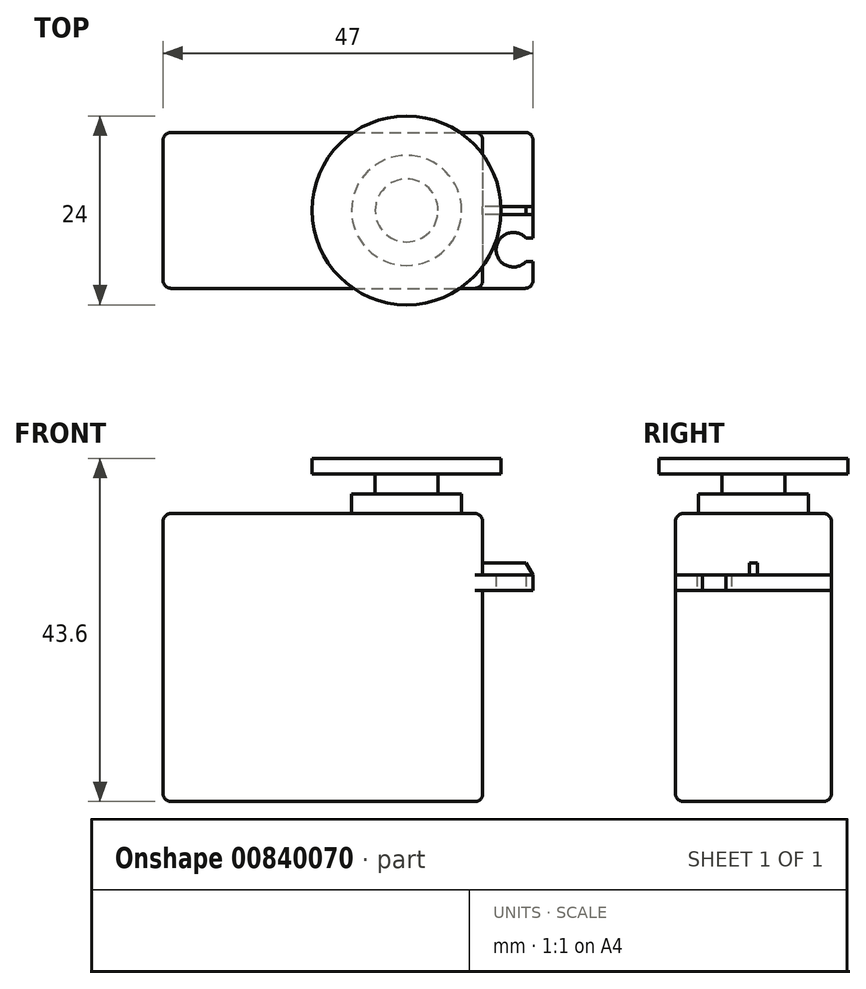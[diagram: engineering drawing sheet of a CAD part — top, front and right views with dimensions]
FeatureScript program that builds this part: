
annotation { "Feature Type Name" : "Feature", "Feature Type Description" : "" }
export const myFeature = defineFeature(function(context is Context, id is Id, definition is map)
    precondition{}
    {
        {
            var Q0;
            Q0=qCreatedBy(makeId("Top.planeOp"),FACE);
            cPlane(context, id + "F0", {"entities" : qUnion([Q0]), "cplaneType" : CPlaneType.OFFSET, "offset" : 26.8 * mm, "width" : 150 * mm, "height" : 150 * mm});
        }
        {
            var Q0;
            Q0=qCreatedBy(makeId("Top.planeOp"),FACE);
            var sketch = newSketch(context, id + "F1", { "sketchPlane" : qUnion([Q0])});
            skLineSegment(sketch, "E0.bottom", {"start": v(-20.3, 9.9) * mm, "end": v(20.3, 9.9) * mm});
            skLineSegment(sketch, "E0.top", {"start": v(-20.3, -9.9) * mm, "end": v(20.3, -9.9) * mm});
            skLineSegment(sketch, "E0.left", {"start": v(-20.3, 9.9) * mm, "end": v(-20.3, -9.9) * mm});
            skLineSegment(sketch, "E0.right", {"start": v(20.3, 9.9) * mm, "end": v(20.3, -9.9) * mm});
            skSolve(sketch);
        }
        {
            var Q0;
            Q0=makeQuery(id+"F1.imprint","IMPRINT",FACE,{"disambiguationData":[TD([[makeQuery(id+"F1.imprint","IMPRINT",EDGE,{"derivedFrom":sQuery(id+"F1.wireOp",EDGE,"E0.bottom")}),-1.0]])]});
            extrude(context, id + "F2", {"entities" : qUnion([Q0]), "depth" : 36.6 * mm, "offsetDistance" : 25 * mm});
        }
        {
            var Q0;
            Q0=makeQuery(id+"F2.opExtrude","CAP_FACE",FACE,{"disambiguationData":[OSD([sQuery(id+"F1.wireOp",EDGE,"E0.bottom"),sQuery(id+"F1.wireOp",EDGE,"E0.top"),sQuery(id+"F1.wireOp",EDGE,"E0.left"),sQuery(id+"F1.wireOp",EDGE,"E0.right")])],"isStart":false});
            var sketch = newSketch(context, id + "F3", { "sketchPlane" : qUnion([Q0])});
            skCircle(sketch, "E1", {"center": v(10.64, 0) * mm, "radius": 7 * mm});
            skSolve(sketch);
        }
        {
            var Q0;
            Q0 = qSketchRegion(id + "F3", true);
            extrude(context, id + "F4", {"entities" : qUnion([Q0]), "operationType" : NewBodyOperationType.ADD, "depth" : 2.5 * mm, "offsetDistance" : 25 * mm});
        }
        {
            var Q0;
            Q0=makeQuery(id+"F4.opExtrude","CAP_FACE",FACE,{"disambiguationData":[OSD([sQuery(id+"F3.wireOp",EDGE,"E1")])],"isStart":false});
            var sketch = newSketch(context, id + "F5", { "sketchPlane" : qUnion([Q0])});
            skCircle(sketch, "E2", {"center": v(10.64, 0) * mm, "radius": 4 * mm});
            skSolve(sketch);
        }
        {
            var Q0;
            Q0 = qSketchRegion(id + "F5", true);
            extrude(context, id + "F6", {"entities" : qUnion([Q0]), "operationType" : NewBodyOperationType.ADD, "depth" : 2.5 * mm, "offsetDistance" : 25 * mm});
        }
        {
            var Q0;
            Q0=makeQuery(id+"F6.opExtrude","CAP_FACE",FACE,{"disambiguationData":[OSD([sQuery(id+"F5.wireOp",EDGE,"E2")])],"isStart":false});
            var sketch = newSketch(context, id + "F7", { "sketchPlane" : qUnion([Q0])});
            skCircle(sketch, "E3", {"center": v(10.64, 0) * mm, "radius": 12 * mm});
            skSolve(sketch);
        }
        {
            var Q0;
            Q0 = qSketchRegion(id + "F7", true);
            extrude(context, id + "F8", {"entities" : qUnion([Q0]), "operationType" : NewBodyOperationType.ADD, "depth" : 2 * mm, "offsetDistance" : 25 * mm});
        }
        {
            var Q0;
            {var subQ0=sQuery(id+"F1.wireOp",EDGE,"E0.bottom");var subQ1=sQuery(id+"F1.wireOp",EDGE,"E0.right");var subQ2=sQuery(id+"F1.wireOp",EDGE,"E0.top");Q0=makeQuery(id+"F11.boolean.opBoolean","SPLIT",FACE,{"disambiguationData":[TD([makeQuery(id+"F2.opExtrude","CAP_FACE",FACE,{"disambiguationData":[OSD([subQ0,subQ2,sQuery(id+"F1.wireOp",EDGE,"E0.left"),subQ1])],"isStart":true})])],"derivedFrom":makeQuery(id+"F2.opExtrude","SWEPT_FACE",FACE,{"disambiguationData":[OSD([subQ1])]})});}
            cPlane(context, id + "F9", {"entities" : qUnion([Q0]), "cplaneType" : CPlaneType.OFFSET, "offset" : 0 * mm, "width" : 150 * mm, "height" : 150 * mm});
        }
        {
            var Q0;
            Q0=qCreatedBy(id+"F0.planeOp",FACE);
            var sketch = newSketch(context, id + "F10", { "sketchPlane" : qUnion([Q0])});
            skLineSegment(sketch, "E4.bottom", {"start": v(20.3, 9.9) * mm, "end": v(26.7, 9.9) * mm});
            skLineSegment(sketch, "E4.top", {"start": v(20.3, -9.9) * mm, "end": v(26.7, -9.9) * mm});
            skLineSegment(sketch, "E4.left", {"start": v(20.3, 9.9) * mm, "end": v(20.3, -9.9) * mm});
            skLineSegment(sketch, "E4.right", {"start": v(26.7, 9.9) * mm, "end": v(26.7, -9.9) * mm});
            skSolve(sketch);
        }
        {
            var Q0;
            Q0 = qSketchRegion(id + "F10", true);
            extrude(context, id + "F11", {"entities" : qUnion([Q0]), "operationType" : NewBodyOperationType.ADD, "depth" : 2 * mm, "offsetDistance" : 25 * mm});
        }
        {
            var Q0;
            Q0=qCreatedBy(id+"F0.planeOp",FACE);
            var sketch = newSketch(context, id + "F12", { "sketchPlane" : qUnion([Q0])});
            skPoint(sketch, "E5", {"position": v(24.2, -5) * mm});
            skArc(sketch, "E6", {"start": v(25.8, -3.5) * mm, "mid": v(22, -5) * mm, "end": v(25.8, -6.5) * mm});
            skLineSegment(sketch, "E7", {"start": v(25.8, -3.5) * mm, "end": v(26.7, -3.5) * mm});
            skLineSegment(sketch, "E8", {"start": v(26.7, -3.5) * mm, "end": v(26.7, -6.5) * mm});
            skLineSegment(sketch, "E9", {"start": v(26.7, -6.5) * mm, "end": v(25.8, -6.5) * mm});
            skLineSegment(sketch, "E10", {"start": v(24.2, -5) * mm, "end": v(29.03, -5) * mm, "construction": true});
            skSolve(sketch);
        }
        {
            var Q0;
            Q0 = qSketchRegion(id + "F12", true);
            extrude(context, id + "F13", {"entities" : qUnion([Q0]), "operationType" : NewBodyOperationType.REMOVE, "depth" : 4 * mm, "offsetDistance" : 25 * mm});
        }
        {
            var Q0;
            {var subQ1=sQuery(id+"F1.wireOp",EDGE,"E0.left");var subQ2=sQuery(id+"F1.wireOp",EDGE,"E0.top");Q0=makeQuery(id+"FE7LxPU3QRs9F0V_1.1.F11.boolean.opBoolean","SPLIT",EDGE,{"disambiguationData":[TD([makeQuery(id+"F2.opExtrude","CAP_FACE",FACE,{"disambiguationData":[OSD([sQuery(id+"F1.wireOp",EDGE,"E0.bottom"),subQ2,subQ1,sQuery(id+"F1.wireOp",EDGE,"E0.right")])],"isStart":true})])],"derivedFrom":makeQuery(id+"F2.opExtrude","SWEPT_EDGE",EDGE,{"disambiguationData":[OSD([subQ2,subQ1])]})});}
            var Q1;
            Q1=makeQuery(id+"F2.opExtrude","CAP_EDGE",EDGE,{"disambiguationData":[OSD([sQuery(id+"F1.wireOp",EDGE,"E0.top")])],"isStart":true});
            var Q2;
            Q2=makeQuery(id+"F2.opExtrude","CAP_EDGE",EDGE,{"disambiguationData":[OSD([sQuery(id+"F1.wireOp",EDGE,"E0.left")])],"isStart":true});
            var Q3;
            {var subQ0=sQuery(id+"F1.wireOp",EDGE,"E0.left");var subQ2=sQuery(id+"F1.wireOp",EDGE,"E0.bottom");Q3=makeQuery(id+"FE7LxPU3QRs9F0V_1.1.F11.boolean.opBoolean","SPLIT",EDGE,{"disambiguationData":[TD([makeQuery(id+"F2.opExtrude","CAP_FACE",FACE,{"disambiguationData":[OSD([subQ2,sQuery(id+"F1.wireOp",EDGE,"E0.top"),subQ0,sQuery(id+"F1.wireOp",EDGE,"E0.right")])],"isStart":true})])],"derivedFrom":makeQuery(id+"F2.opExtrude","SWEPT_EDGE",EDGE,{"disambiguationData":[OSD([subQ2,subQ0])]})});}
            var Q4;
            Q4=makeQuery(id+"F2.opExtrude","CAP_EDGE",EDGE,{"disambiguationData":[OSD([sQuery(id+"F1.wireOp",EDGE,"E0.bottom")])],"isStart":true});
            var Q5;
            Q5=makeQuery(id+"F2.opExtrude","CAP_EDGE",EDGE,{"disambiguationData":[OSD([sQuery(id+"F1.wireOp",EDGE,"E0.right")])],"isStart":true});
            var Q6;
            {var subQ1=sQuery(id+"F1.wireOp",EDGE,"E0.right");var subQ2=sQuery(id+"F1.wireOp",EDGE,"E0.bottom");Q6=makeQuery(id+"F11.boolean.opBoolean","SPLIT",EDGE,{"disambiguationData":[TD([makeQuery(id+"F2.opExtrude","CAP_FACE",FACE,{"disambiguationData":[OSD([subQ2,sQuery(id+"F1.wireOp",EDGE,"E0.top"),sQuery(id+"F1.wireOp",EDGE,"E0.left"),subQ1])],"isStart":true})])],"derivedFrom":makeQuery(id+"F2.opExtrude","SWEPT_EDGE",EDGE,{"disambiguationData":[OSD([subQ2,subQ1])]})});}
            var Q7;
            {var subQ1=sQuery(id+"F1.wireOp",EDGE,"E0.right");var subQ2=sQuery(id+"F1.wireOp",EDGE,"E0.top");Q7=makeQuery(id+"F11.boolean.opBoolean","SPLIT",EDGE,{"disambiguationData":[TD([makeQuery(id+"F2.opExtrude","CAP_FACE",FACE,{"disambiguationData":[OSD([sQuery(id+"F1.wireOp",EDGE,"E0.bottom"),subQ2,sQuery(id+"F1.wireOp",EDGE,"E0.left"),subQ1])],"isStart":true})])],"derivedFrom":makeQuery(id+"F2.opExtrude","SWEPT_EDGE",EDGE,{"disambiguationData":[OSD([subQ2,subQ1])]})});}
            var Q8;
            {var subQ1=sQuery(id+"F1.wireOp",EDGE,"E0.left");var subQ2=sQuery(id+"F1.wireOp",EDGE,"E0.bottom");Q8=makeQuery(id+"FE7LxPU3QRs9F0V_1.1.F11.boolean.opBoolean","SPLIT",EDGE,{"disambiguationData":[TD([makeQuery(id+"F2.opExtrude","CAP_FACE",FACE,{"disambiguationData":[OSD([subQ2,sQuery(id+"F1.wireOp",EDGE,"E0.top"),subQ1,sQuery(id+"F1.wireOp",EDGE,"E0.right")])],"isStart":false})])],"derivedFrom":makeQuery(id+"F2.opExtrude","SWEPT_EDGE",EDGE,{"disambiguationData":[OSD([subQ2,subQ1])]})});}
            var Q9;
            Q9=makeQuery(id+"F2.opExtrude","CAP_EDGE",EDGE,{"disambiguationData":[OSD([sQuery(id+"F1.wireOp",EDGE,"E0.left")])],"isStart":false});
            var Q10;
            Q10=makeQuery(id+"F2.opExtrude","CAP_EDGE",EDGE,{"disambiguationData":[OSD([sQuery(id+"F1.wireOp",EDGE,"E0.bottom")])],"isStart":false});
            var Q11;
            Q11=makeQuery(id+"F2.opExtrude","CAP_EDGE",EDGE,{"disambiguationData":[OSD([sQuery(id+"F1.wireOp",EDGE,"E0.top")])],"isStart":false});
            var Q12;
            {var subQ1=sQuery(id+"F1.wireOp",EDGE,"E0.left");var subQ2=sQuery(id+"F1.wireOp",EDGE,"E0.top");Q12=makeQuery(id+"FE7LxPU3QRs9F0V_1.1.F11.boolean.opBoolean","SPLIT",EDGE,{"disambiguationData":[TD([makeQuery(id+"F2.opExtrude","CAP_FACE",FACE,{"disambiguationData":[OSD([sQuery(id+"F1.wireOp",EDGE,"E0.bottom"),subQ2,subQ1,sQuery(id+"F1.wireOp",EDGE,"E0.right")])],"isStart":false})])],"derivedFrom":makeQuery(id+"F2.opExtrude","SWEPT_EDGE",EDGE,{"disambiguationData":[OSD([subQ2,subQ1])]})});}
            var Q13;
            {var subQ0=sQuery(id+"F1.wireOp",EDGE,"E0.right");var subQ2=sQuery(id+"F1.wireOp",EDGE,"E0.top");Q13=makeQuery(id+"F11.boolean.opBoolean","SPLIT",EDGE,{"disambiguationData":[TD([makeQuery(id+"F2.opExtrude","CAP_FACE",FACE,{"disambiguationData":[OSD([sQuery(id+"F1.wireOp",EDGE,"E0.bottom"),subQ2,sQuery(id+"F1.wireOp",EDGE,"E0.left"),subQ0])],"isStart":false})])],"derivedFrom":makeQuery(id+"F2.opExtrude","SWEPT_EDGE",EDGE,{"disambiguationData":[OSD([subQ2,subQ0])]})});}
            var Q14;
            Q14=makeQuery(id+"F2.opExtrude","CAP_EDGE",EDGE,{"disambiguationData":[OSD([sQuery(id+"F1.wireOp",EDGE,"E0.right")])],"isStart":false});
            var Q15;
            {var subQ1=sQuery(id+"F1.wireOp",EDGE,"E0.right");var subQ2=sQuery(id+"F1.wireOp",EDGE,"E0.bottom");Q15=makeQuery(id+"F11.boolean.opBoolean","SPLIT",EDGE,{"disambiguationData":[TD([makeQuery(id+"F2.opExtrude","CAP_FACE",FACE,{"disambiguationData":[OSD([subQ2,sQuery(id+"F1.wireOp",EDGE,"E0.top"),sQuery(id+"F1.wireOp",EDGE,"E0.left"),subQ1])],"isStart":false})])],"derivedFrom":makeQuery(id+"F2.opExtrude","SWEPT_EDGE",EDGE,{"disambiguationData":[OSD([subQ2,subQ1])]})});}
            var Q16;
            Q16=makeQuery(id+"F11.opExtrude","SWEPT_EDGE",EDGE,{"disambiguationData":[OSD([sQuery(id+"F10.wireOp",EDGE,"E4.top"),sQuery(id+"F10.wireOp",EDGE,"E4.right")])]});
            var Q17;
            Q17=makeQuery(id+"F11.opExtrude","SWEPT_EDGE",EDGE,{"disambiguationData":[OSD([sQuery(id+"F10.wireOp",EDGE,"E4.bottom"),sQuery(id+"F10.wireOp",EDGE,"E4.right")])]});
            var Q18;
            Q18=makeQuery(id+"FE7LxPU3QRs9F0V_1.1.F11.opExtrude","SWEPT_EDGE",EDGE,{"disambiguationData":[OSD([sQuery(id+"F10.wireOp",EDGE,"E4.bottom"),sQuery(id+"F10.wireOp",EDGE,"E4.right")])]});
            var Q19;
            Q19=makeQuery(id+"FE7LxPU3QRs9F0V_1.1.F11.opExtrude","SWEPT_EDGE",EDGE,{"disambiguationData":[OSD([sQuery(id+"F10.wireOp",EDGE,"E4.top"),sQuery(id+"F10.wireOp",EDGE,"E4.right")])]});
            fillet(context, id + "F14", {"entities" : qUnion([Q0, Q1, Q2, Q3, Q4, Q5, Q6, Q7, Q8, Q9, Q10, Q11, Q12, Q13, Q14, Q15, Q16, Q17, Q18, Q19]), "radius" : 1 * mm, "tangentPropagation" : true, "allowEdgeOverflow" : false});
        }
        {
            var Q0;
            Q0=qCreatedBy(makeId("Front.planeOp"),FACE);
            var sketch = newSketch(context, id + "F15", { "sketchPlane" : qUnion([Q0])});
            skLineSegment(sketch, "E11", {"start": v(25.83, 30.3) * mm, "end": v(26.7, 28.8) * mm});
            skLineSegment(sketch, "E12", {"start": v(26.7, 28.8) * mm, "end": v(20.3, 28.8) * mm});
            skLineSegment(sketch, "E13", {"start": v(20.3, 30.3) * mm, "end": v(20.3, 28.8) * mm});
            skLineSegment(sketch, "E14", {"start": v(25.83, 30.3) * mm, "end": v(20.3, 30.3) * mm});
            skSolve(sketch);
        }
        {
            var Q0;
            Q0 = qSketchRegion(id + "F15", true);
            extrude(context, id + "F16", {"entities" : qUnion([Q0]), "operationType" : NewBodyOperationType.ADD, "endBound" : BoundingType.SYMMETRIC, "depth" : 1 * mm, "offsetDistance" : 25 * mm});
        }
    });
